FCSTD DOCUMENT  (FreeCAD 1.1R39747 (Git))
Label: SelfTapTest
License: All rights reserved
LicenseURL: https://en.wikipedia.org/wiki/All_rights_reserved
objects: App::Point×1, Sketcher::SketchObject×1, PartDesign::Body×1
note: 3 computed .brp shape members not serialized (recipe doc carries the construction recipe); baked Part::Feature solids carry a one-line shape summary decoded from their .brp

FEATURE [App::Point] Origin001
  Role = Origin
FEATURE [Sketcher::SketchObject] Sketch
  ArcFitTolerance = 1e-06
  AttachmentSupport = -> [XY_Plane]
  ExternalTypes = [0]
  FullyConstrained = true
  MakeInternals = false
  MapMode = 5
  expr: Constraints[13] = 5
  sketch-geometry (11):
    g0: LineSegment StartX=-50 StartY=-12.5 StartZ=0 EndX=50 EndY=-12.5 EndZ=0
    g1: LineSegment StartX=50 StartY=-12.5 StartZ=0 EndX=50 EndY=12.5 EndZ=0
    g2: LineSegment StartX=50 StartY=12.5 StartZ=0 EndX=-50 EndY=12.5 EndZ=0
    g3: LineSegment StartX=-50 StartY=12.5 StartZ=0 EndX=-50 EndY=-12.5 EndZ=0
    g4: GeomPoint [constr] X=-6.5e-15 Y=2.8315e-12 Z=0
    g5: Circle CenterX=-6.5e-15 CenterY=2.8315e-12 CenterZ=0 NormalX=0 NormalY=0 NormalZ=1 AngleXU=0 Radius=2.5
    g6: LineSegment [constr] StartX=-3.8e-15 StartY=-2.5 StartZ=0 EndX=-3.8e-15 EndY=-2.25 EndZ=0
    g7: ArcOfCircle CenterX=-3.8e-15 CenterY=-2.25 CenterZ=0 NormalX=0 NormalY=0 NormalZ=1 AngleXU=0 Radius=0.5 StartAngle=0 EndAngle=3.14159
    g8: LineSegment StartX=0.5 StartY=-2.25 StartZ=0 EndX=0.5 EndY=-2.44949 EndZ=0
    g9: LineSegment StartX=-0.5 StartY=-2.25 StartZ=0 EndX=-0.5 EndY=-2.44949 EndZ=0
    g10: Circle [constr] CenterX=-6.5e-15 CenterY=2.8315e-12 CenterZ=0 NormalX=0 NormalY=0 NormalZ=1 AngleXU=0 Radius=1.75
  constraints (30):
    c: Coincident(g0,g1)
    c: Coincident(g1,g2)
    c: Coincident(g2,g3)
    c: Coincident(g3,g0)
    c: Horizontal(g0)
    c: Horizontal(g2)
    c: Vertical(g1)
    c: Vertical(g3)
    c: Symmetric(g2,g0,g4)
    c: Distance(g1,g3) = 100
    c: Distance(g0,g2) = 25
    c: Coincident(g4,g-1)
    c: Coincident(g5,g4)
    c: Diameter(g5) = 5
    c: PointOnObject(g6,g5)
    c: Vertical(g6)
    c: PointOnObject(g6,g-2)
    c: Coincident(g7,g6)
    c: Horizontal(g7,g6)
    c: Coincident(g8,g7)
    c: PointOnObject(g8,g5)
    c: Vertical(g8)
    c: Coincident(g9,g7)
    c: PointOnObject(g9,g5)
    c: Vertical(g9)
    c: Coincident(g10,g4)
    c: Tangent(g10,g7)
    c: Diameter(g10) = 3.5
    c: Radius(g7) = 0.5
    c: Horizontal(g6,g7)
FEATURE [PartDesign::Body] Body
  AllowCompound = true
  Group = -> [Sketch]
  Origin = -> Origin
